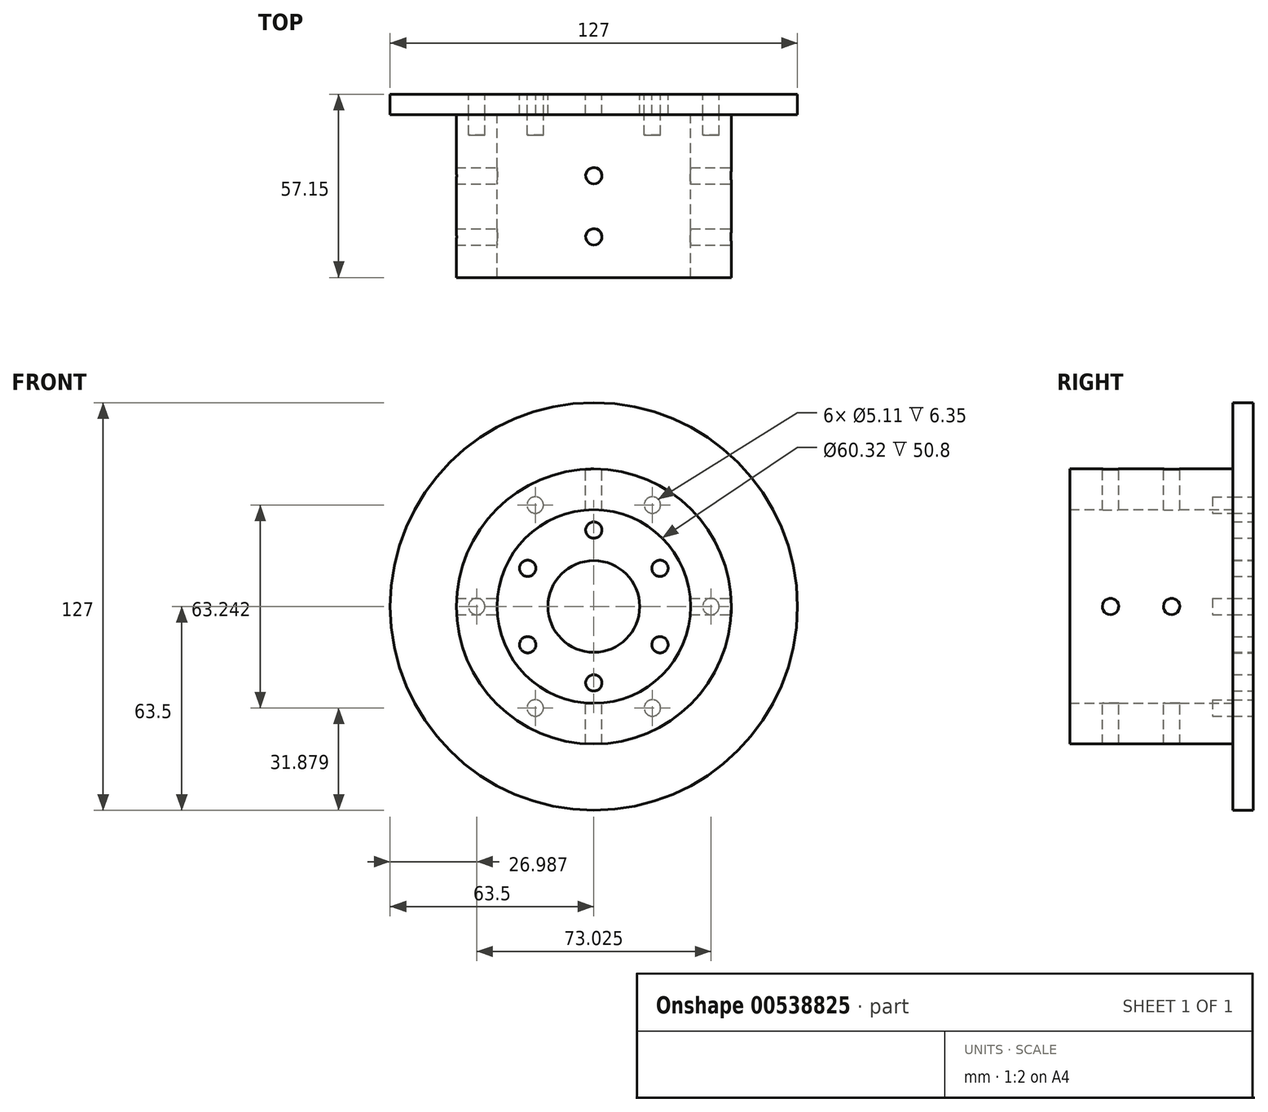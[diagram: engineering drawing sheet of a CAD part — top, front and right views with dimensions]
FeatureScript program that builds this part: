
annotation { "Feature Type Name" : "Feature", "Feature Type Description" : "" }
export const myFeature = defineFeature(function(context is Context, id is Id, definition is map)
    precondition{}
    {
        {
            var Q0;
            Q0=qCreatedBy(makeId("Front.planeOp"),FACE);
            var sketch = newSketch(context, id + "F0", { "sketchPlane" : qUnion([Q0])});
            skCircle(sketch, "E0", {"center": v(0, 0) * mm, "radius": 63.5 * mm});
            skCircle(sketch, "E1", {"center": v(0, 0) * mm, "radius": 23.81 * mm, "construction": true});
            skCircle(sketch, "E2", {"center": v(0, 23.81) * mm, "radius": 2.54 * mm});
            skCircle(sketch, "E3.1.0", {"center": v(-20.62, 11.9) * mm, "radius": 2.54 * mm});
            skCircle(sketch, "E3.2.0", {"center": v(-20.62, -11.9) * mm, "radius": 2.54 * mm});
            skCircle(sketch, "E3.3.0", {"center": v(0, -23.81) * mm, "radius": 2.54 * mm});
            skCircle(sketch, "E3.4.0", {"center": v(20.62, -11.9) * mm, "radius": 2.54 * mm});
            skCircle(sketch, "E3.5.0", {"center": v(20.62, 11.9) * mm, "radius": 2.54 * mm});
            skCircle(sketch, "E4", {"center": v(0, 0) * mm, "radius": 14.29 * mm});
            skCircle(sketch, "E5", {"center": v(0, 0) * mm, "radius": 26.25 * mm, "construction": true});
            skSolve(sketch);
        }
        {
            var Q0;
            Q0=makeQuery(id+"F0.imprint","IMPRINT",FACE,{"disambiguationData":[TD([[makeQuery(id+"F0.imprint","IMPRINT",EDGE,{"derivedFrom":sQuery(id+"F0.wireOp",EDGE,"E0")}),1.0]])]});
            extrude(context, id + "F1", {"entities" : qUnion([Q0]), "depth" : 6.35 * mm, "offsetDistance" : 25.4 * mm});
        }
        {
            var Q0;
            Q0=makeQuery(id+"F1.opExtrude","CAP_FACE",FACE,{"disambiguationData":[OSD([sQuery(id+"F0.wireOp",EDGE,"tUyqgp1G-GTFX-5wIg-Lo9G-vFgwfLQDsMrt"),sQuery(id+"F0.wireOp",EDGE,"E0")])],"isStart":false});
            var sketch = newSketch(context, id + "F2", { "sketchPlane" : qUnion([Q0])});
            skCircle(sketch, "E6", {"center": v(0, 0) * mm, "radius": 30.16 * mm});
            skCircle(sketch, "E7", {"center": v(0, 0) * mm, "radius": 42.86 * mm});
            skSolve(sketch);
        }
        {
            var Q0;
            Q0 = qSketchRegion(id + "F2", true);
            extrude(context, id + "F3", {"entities" : qUnion([Q0]), "depth" : 50.8 * mm, "offsetDistance" : 25.4 * mm});
        }
        {
            var Q0;
            Q0=qCreatedBy(makeId("Right.planeOp"),FACE);
            cPlane(context, id + "F4", {"entities" : qUnion([Q0]), "cplaneType" : CPlaneType.OFFSET, "offset" : 45.2 * mm, "width" : 152.4 * mm, "height" : 152.4 * mm});
        }
        {
            var Q0;
            Q0=qCreatedBy(id+"F4.planeOp",FACE);
            var sketch = newSketch(context, id + "F5", { "sketchPlane" : qUnion([Q0])});
            skCircle(sketch, "E8", {"center": v(-25.4, 0) * mm, "radius": 2.54 * mm});
            skCircle(sketch, "E9", {"center": v(-44.45, 0) * mm, "radius": 2.54 * mm});
            skSolve(sketch);
        }
        {
            var Q0;
            Q0=makeQuery(id+"F5.imprint","IMPRINT",FACE,{"disambiguationData":[TD([[makeQuery(id+"F5.imprint","IMPRINT",EDGE,{"derivedFrom":sQuery(id+"F5.wireOp",EDGE,"E8")}),1.0]])]});
            var Q1;
            Q1=makeQuery(id+"F5.imprint","IMPRINT",FACE,{"disambiguationData":[TD([[makeQuery(id+"F5.imprint","IMPRINT",EDGE,{"derivedFrom":sQuery(id+"F5.wireOp",EDGE,"E9")}),1.0]])]});
            var Q2;
            Q2=makeQuery(id+"FNfUYekIyvd2Eg9_0.opExtrude","SWEPT_FACE",FACE,{"disambiguationData":[OSD([sQuery(id+"F0.wireOp",EDGE,"tUyqgp1G-GTFX-5wIg-Lo9G-vFgwfLQDsMrt")])]});
            extrude(context, id + "F6", {"entities" : qUnion([Q0, Q1]), "operationType" : NewBodyOperationType.REMOVE, "oppositeDirection" : true, "depth" : 101.6 * mm, "endBoundEntityFace" : qUnion([Q2]), "offsetDistance" : 25.4 * mm});
        }
        {
            var Q0;
            Q0=qCreatedBy(makeId("Top.planeOp"),FACE);
            cPlane(context, id + "F7", {"entities" : qUnion([Q0]), "cplaneType" : CPlaneType.OFFSET, "offset" : 44.2 * mm, "width" : 152.4 * mm, "height" : 152.4 * mm});
        }
        {
            var Q0;
            Q0=qCreatedBy(id+"F7.planeOp",FACE);
            var sketch = newSketch(context, id + "F8", { "sketchPlane" : qUnion([Q0])});
            skCircle(sketch, "E10", {"center": v(0, -25.4) * mm, "radius": 2.54 * mm});
            skCircle(sketch, "E11", {"center": v(0, -44.45) * mm, "radius": 2.54 * mm});
            skSolve(sketch);
        }
        {
            var Q0;
            Q0=makeQuery(id+"F8.imprint","IMPRINT",FACE,{"disambiguationData":[TD([[makeQuery(id+"F8.imprint","IMPRINT",EDGE,{"derivedFrom":sQuery(id+"F8.wireOp",EDGE,"E10")}),1.0]])]});
            var Q1;
            Q1=makeQuery(id+"F8.imprint","IMPRINT",FACE,{"disambiguationData":[TD([[makeQuery(id+"F8.imprint","IMPRINT",EDGE,{"derivedFrom":sQuery(id+"F8.wireOp",EDGE,"E11")}),1.0]])]});
            extrude(context, id + "F9", {"entities" : qUnion([Q0, Q1]), "operationType" : NewBodyOperationType.REMOVE, "oppositeDirection" : true, "depth" : 101.6 * mm, "offsetDistance" : 25.4 * mm});
        }
        {
            var Q0;
            Q0=makeQuery(id+"F1.opExtrude","CAP_FACE",FACE,{"disambiguationData":[OSD([sQuery(id+"F0.wireOp",EDGE,"E0"),sQuery(id+"F0.wireOp",EDGE,"E2"),sQuery(id+"F0.wireOp",EDGE,"E3.1.0"),sQuery(id+"F0.wireOp",EDGE,"E3.2.0"),sQuery(id+"F0.wireOp",EDGE,"E3.3.0"),sQuery(id+"F0.wireOp",EDGE,"E3.4.0"),sQuery(id+"F0.wireOp",EDGE,"E3.5.0"),sQuery(id+"F0.wireOp",EDGE,"E4")])],"isStart":true});
            var sketch = newSketch(context, id + "F10", { "sketchPlane" : qUnion([Q0])});
            skCircle(sketch, "E12.0", {"center": v(0, 0) * mm, "radius": 30.16 * mm, "construction": true});
            skCircle(sketch, "E13.0", {"center": v(0, 0) * mm, "radius": 42.86 * mm, "construction": true});
            skCircle(sketch, "E14", {"center": v(18.26, 31.62) * mm, "radius": 2.55 * mm});
            skCircle(sketch, "E15.1.0", {"center": v(-18.26, 31.62) * mm, "radius": 2.55 * mm});
            skCircle(sketch, "E15.2.0", {"center": v(-36.51, 0) * mm, "radius": 2.55 * mm});
            skCircle(sketch, "E15.3.0", {"center": v(-18.26, -31.62) * mm, "radius": 2.55 * mm});
            skCircle(sketch, "E15.4.0", {"center": v(18.26, -31.62) * mm, "radius": 2.55 * mm});
            skCircle(sketch, "E15.5.0", {"center": v(36.51, 0) * mm, "radius": 2.55 * mm});
            skSolve(sketch);
        }
        {
            var Q0;
            Q0 = qSketchRegion(id + "F10", true);
            extrude(context, id + "F11", {"entities" : qUnion([Q0]), "operationType" : NewBodyOperationType.REMOVE, "oppositeDirection" : true, "depth" : 12.7 * mm, "offsetDistance" : 25.4 * mm});
        }
    });
